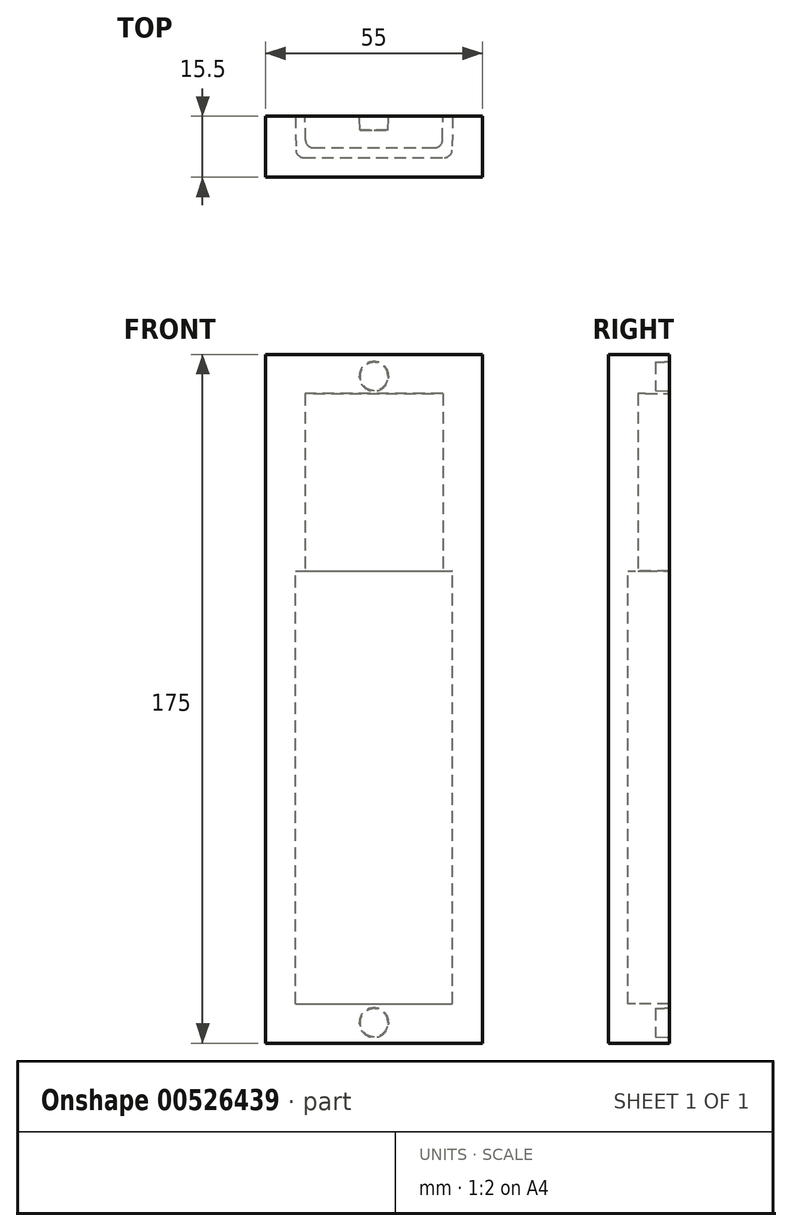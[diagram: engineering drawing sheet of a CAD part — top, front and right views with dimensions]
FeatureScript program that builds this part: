
annotation { "Feature Type Name" : "Feature", "Feature Type Description" : "" }
export const myFeature = defineFeature(function(context is Context, id is Id, definition is map)
    precondition{}
    {
        {
            var Q0;
            Q0=qCreatedBy(makeId("Top.planeOp"),FACE);
            var sketch = newSketch(context, id + "F0", { "sketchPlane" : qUnion([Q0])});
            skLineSegment(sketch, "E0.bottom", {"start": v(25, -13) * mm, "end": v(-25, -13) * mm});
            skLineSegment(sketch, "E0.top", {"start": v(25, 13) * mm, "end": v(-25, 13) * mm});
            skLineSegment(sketch, "E0.left", {"start": v(25, -13) * mm, "end": v(25, 13) * mm});
            skLineSegment(sketch, "E0.right", {"start": v(-25, -13) * mm, "end": v(-25, 13) * mm});
            skPoint(sketch, "E0.middle", {"position": v(0, 0) * mm});
            skSolve(sketch);
        }
        {
            var Q0;
            Q0=qSketchRegion(id+"F0",true);
            extrude(context, id + "F1", {"entities" : qUnion([Q0]), "depth" : 55 * mm, "offsetDistance" : 25 * mm});
        }
        {
            var Q0;
            Q0=makeQuery(id+"F1.opExtrude","CAP_FACE",FACE,{"disambiguationData":[OSD([sQuery(id+"F0.wireOp",EDGE,"E0.bottom"),sQuery(id+"F0.wireOp",EDGE,"E0.top"),sQuery(id+"F0.wireOp",EDGE,"E0.left"),sQuery(id+"F0.wireOp",EDGE,"E0.right")])],"isStart":true});
            var sketch = newSketch(context, id + "F2", { "sketchPlane" : qUnion([Q0])});
            skPoint(sketch, "E1.middle", {"position": v(0, 0) * mm});
            skLineSegment(sketch, "E2", {"start": v(17.36, -8) * mm, "end": v(17.5, 0) * mm});
            skLineSegment(sketch, "E3", {"start": v(-17.36, -8) * mm, "end": v(-17.5, 0) * mm});
            skLineSegment(sketch, "E4", {"start": v(-17.36, 8) * mm, "end": v(-17.5, 0) * mm});
            skLineSegment(sketch, "E5", {"start": v(17.36, 8) * mm, "end": v(17.5, 0) * mm});
            skLineSegment(sketch, "E6", {"start": v(-17.36, 8) * mm, "end": v(17.36, 8) * mm});
            skLineSegment(sketch, "E7", {"start": v(-17.36, -8) * mm, "end": v(17.36, -8) * mm});
            skSolve(sketch);
        }
        {
            var Q0;
            Q0=qSketchRegion(id+"F2",true);
            extrude(context, id + "F3", {"entities" : qUnion([Q0]), "operationType" : NewBodyOperationType.REMOVE, "oppositeDirection" : true, "depth" : 45 * mm, "offsetDistance" : 25 * mm});
        }
        {
            var Q0;
            Q0=makeQuery(id+"F3.boolean.opBoolean","COPY",EDGE,{"derivedFrom":makeQuery(id+"F3.opExtrude","SWEPT_EDGE",EDGE,{"disambiguationData":[OSD([sQuery(id+"F2.wireOp",EDGE,"E3"),sQuery(id+"F2.wireOp",EDGE,"E7")])]})});
            var Q1;
            Q1=makeQuery(id+"F3.boolean.opBoolean","COPY",EDGE,{"derivedFrom":makeQuery(id+"F3.opExtrude","SWEPT_EDGE",EDGE,{"disambiguationData":[OSD([sQuery(id+"F2.wireOp",EDGE,"E2"),sQuery(id+"F2.wireOp",EDGE,"E7")])]})});
            fillet(context, id + "F4", {"entities" : qUnion([Q0, Q1]), "radius" : 2 * mm, "tangentPropagation" : true, "allowEdgeOverflow" : false});
        }
        {
            var Q0;
            Q0=makeQuery(id+"F3.boolean.opBoolean","COPY",EDGE,{"derivedFrom":makeQuery(id+"F3.opExtrude","SWEPT_EDGE",EDGE,{"disambiguationData":[OSD([sQuery(id+"F2.wireOp",EDGE,"E4"),sQuery(id+"F2.wireOp",EDGE,"E6")])]})});
            var Q1;
            Q1=makeQuery(id+"F3.boolean.opBoolean","COPY",EDGE,{"derivedFrom":makeQuery(id+"F3.opExtrude","SWEPT_EDGE",EDGE,{"disambiguationData":[OSD([sQuery(id+"F2.wireOp",EDGE,"E5"),sQuery(id+"F2.wireOp",EDGE,"E6")])]})});
            fillet(context, id + "F5", {"entities" : qUnion([Q0, Q1]), "radius" : 2 * mm, "tangentPropagation" : true, "allowEdgeOverflow" : false});
        }
        {
            var Q0;
            Q0=makeQuery(id+"F1.opExtrude","CAP_FACE",FACE,{"disambiguationData":[OSD([sQuery(id+"F0.wireOp",EDGE,"E0.bottom"),sQuery(id+"F0.wireOp",EDGE,"E0.top"),sQuery(id+"F0.wireOp",EDGE,"E0.left"),sQuery(id+"F0.wireOp",EDGE,"E0.right")])],"isStart":true});
            var sketch = newSketch(context, id + "F6", { "sketchPlane" : qUnion([Q0])});
            skLineSegment(sketch, "E8.bottom", {"start": v(27.5, -15.5) * mm, "end": v(-27.5, -15.5) * mm});
            skLineSegment(sketch, "E8.top", {"start": v(27.5, 15.5) * mm, "end": v(-27.5, 15.5) * mm});
            skLineSegment(sketch, "E8.left", {"start": v(27.5, -15.5) * mm, "end": v(27.5, 15.5) * mm});
            skLineSegment(sketch, "E8.right", {"start": v(-27.5, -15.5) * mm, "end": v(-27.5, 15.5) * mm});
            skPoint(sketch, "E8.middle", {"position": v(0, 0) * mm});
            skSolve(sketch);
        }
        {
            var Q0;
            Q0=qSketchRegion(id+"F6",true);
            extrude(context, id + "F7", {"entities" : qUnion([Q0]), "operationType" : NewBodyOperationType.ADD, "depth" : 120 * mm, "offsetDistance" : 25 * mm});
        }
        {
            var Q0;
            {var subQ0=sQuery(id+"F6.wireOp",EDGE,"E8.bottom");var subQ1=sQuery(id+"F6.wireOp",EDGE,"E8.top");var subQ2=sQuery(id+"F6.wireOp",EDGE,"E8.left");var subQ3=sQuery(id+"F6.wireOp",EDGE,"E8.right");Q0=makeQuery(id+"F7.boolean.opBoolean","SPLIT",FACE,{"disambiguationData":[TD([makeQuery(id+"F1.opExtrude","SWEPT_FACE",FACE,{"disambiguationData":[OSD([sQuery(id+"F0.wireOp",EDGE,"E0.bottom")])]})])],"derivedFrom":makeQuery(id+"F7.opExtrude","CAP_FACE",FACE,{"disambiguationData":[OSD([subQ0,subQ1,subQ2,subQ3])],"isStart":true})});}
            var sketch = newSketch(context, id + "F8", { "sketchPlane" : qUnion([Q0])});
            skPoint(sketch, "E9.middle", {"position": v(0, 0) * mm});
            skLineSegment(sketch, "E10", {"start": v(-20, 0) * mm, "end": v(-19.82, -10.5) * mm});
            skLineSegment(sketch, "E11", {"start": v(20, 0) * mm, "end": v(19.82, -10.5) * mm});
            skLineSegment(sketch, "E12", {"start": v(19.82, 10.5) * mm, "end": v(20, 0) * mm});
            skLineSegment(sketch, "E13", {"start": v(-20, 0) * mm, "end": v(-19.82, 10.5) * mm});
            skLineSegment(sketch, "E14", {"start": v(-19.82, -10.5) * mm, "end": v(19.82, -10.5) * mm});
            skLineSegment(sketch, "E15", {"start": v(-19.82, 10.5) * mm, "end": v(19.82, 10.5) * mm});
            skSolve(sketch);
        }
        {
            var Q0;
            Q0=qSketchRegion(id+"F8",true);
            extrude(context, id + "F9", {"entities" : qUnion([Q0]), "operationType" : NewBodyOperationType.REMOVE, "oppositeDirection" : true, "depth" : 110 * mm, "offsetDistance" : 25 * mm});
        }
        {
            var Q0;
            Q0=makeQuery(id+"F9.boolean.opBoolean","COPY",EDGE,{"derivedFrom":makeQuery(id+"F9.opExtrude","SWEPT_EDGE",EDGE,{"disambiguationData":[OSD([sQuery(id+"F8.wireOp",EDGE,"E10"),sQuery(id+"F8.wireOp",EDGE,"E14")])]})});
            var Q1;
            Q1=makeQuery(id+"F9.boolean.opBoolean","COPY",EDGE,{"derivedFrom":makeQuery(id+"F9.opExtrude","SWEPT_EDGE",EDGE,{"disambiguationData":[OSD([sQuery(id+"F8.wireOp",EDGE,"E11"),sQuery(id+"F8.wireOp",EDGE,"E14")])]})});
            var Q2;
            Q2=makeQuery(id+"F9.boolean.opBoolean","COPY",EDGE,{"derivedFrom":makeQuery(id+"F9.opExtrude","SWEPT_EDGE",EDGE,{"disambiguationData":[OSD([sQuery(id+"F8.wireOp",EDGE,"E13"),sQuery(id+"F8.wireOp",EDGE,"E15")])]})});
            var Q3;
            Q3=makeQuery(id+"F9.boolean.opBoolean","COPY",EDGE,{"derivedFrom":makeQuery(id+"F9.opExtrude","SWEPT_EDGE",EDGE,{"disambiguationData":[OSD([sQuery(id+"F8.wireOp",EDGE,"E12"),sQuery(id+"F8.wireOp",EDGE,"E15")])]})});
            fillet(context, id + "F10", {"entities" : qUnion([Q0, Q1, Q2, Q3]), "radius" : 2 * mm, "tangentPropagation" : true, "allowEdgeOverflow" : false});
        }
        {
            var Q0;
            Q0=qCreatedBy(makeId("Front.planeOp"),FACE);
            var sketch = newSketch(context, id + "F11", { "sketchPlane" : qUnion([Q0])});
            skLineSegment(sketch, "E16.bottom", {"start": v(-94.89, 86.67) * mm, "end": v(98.98, 86.67) * mm});
            skLineSegment(sketch, "E16.top", {"start": v(-94.89, -148.46) * mm, "end": v(98.98, -148.46) * mm});
            skLineSegment(sketch, "E16.left", {"start": v(-94.89, 86.67) * mm, "end": v(-94.89, -148.46) * mm});
            skLineSegment(sketch, "E16.right", {"start": v(98.98, 86.67) * mm, "end": v(98.98, -148.46) * mm});
            skSolve(sketch);
        }
        {
            var Q0;
            Q0=qSketchRegion(id+"F11",true);
            extrude(context, id + "F12", {"entities" : qUnion([Q0]), "operationType" : NewBodyOperationType.REMOVE, "endBound" : BoundingType.THROUGH_ALL, "oppositeDirection" : true, "depth" : 25 * mm, "offsetDistance" : 25 * mm});
        }
        {
            var Q0;
            Q0=makeQuery(id+"F12.boolean.opBoolean","COPY",FACE,{"derivedFrom":makeQuery(id+"F12.opExtrude","CAP_FACE",FACE,{"disambiguationData":[OSD([sQuery(id+"F11.wireOp",EDGE,"E16.bottom"),sQuery(id+"F11.wireOp",EDGE,"E16.top"),sQuery(id+"F11.wireOp",EDGE,"E16.left"),sQuery(id+"F11.wireOp",EDGE,"E16.right")])],"isStart":true})});
            var sketch = newSketch(context, id + "F13", { "sketchPlane" : qUnion([Q0])});
            skCircle(sketch, "E17", {"center": v(0, 49.44) * mm, "radius": 3.75 * mm});
            skCircle(sketch, "E18", {"center": v(0, -114.77) * mm, "radius": 3.75 * mm});
            skSolve(sketch);
        }
        {
            var Q0;
            Q0=makeQuery(id+"F13.imprint","IMPRINT",FACE,{"disambiguationData":[TD([[makeQuery(id+"F13.imprint","IMPRINT",EDGE,{"derivedFrom":sQuery(id+"F13.wireOp",EDGE,"E17")}),1.0]])]});
            var Q1;
            Q1=makeQuery(id+"F13.imprint","IMPRINT",FACE,{"disambiguationData":[TD([[makeQuery(id+"F13.imprint","IMPRINT",EDGE,{"derivedFrom":sQuery(id+"F13.wireOp",EDGE,"E18")}),1.0]])]});
            extrude(context, id + "F14", {"entities" : qUnion([Q0, Q1]), "operationType" : NewBodyOperationType.REMOVE, "oppositeDirection" : true, "depth" : 3.5 * mm, "offsetDistance" : 25 * mm, "hasDraft" : true, "draftAngle" : 3 * degree, "draftPullDirection" : true});
        }
        {
            var Q0;
            {var subQ0=sQuery(id+"F6.wireOp",EDGE,"E8.bottom");var subQ1=sQuery(id+"F6.wireOp",EDGE,"E8.top");var subQ2=sQuery(id+"F6.wireOp",EDGE,"E8.left");var subQ3=sQuery(id+"F6.wireOp",EDGE,"E8.right");Q0=makeQuery(id+"F7.boolean.opBoolean","SPLIT",FACE,{"disambiguationData":[TD([makeQuery(id+"F1.opExtrude","SWEPT_FACE",FACE,{"disambiguationData":[OSD([sQuery(id+"F0.wireOp",EDGE,"E0.bottom")])]})])],"derivedFrom":makeQuery(id+"F7.opExtrude","CAP_FACE",FACE,{"disambiguationData":[OSD([subQ0,subQ1,subQ2,subQ3])],"isStart":true})});}
            var Q1;
            Q1=makeQuery(id+"F1.opExtrude","CAP_FACE",FACE,{"disambiguationData":[OSD([sQuery(id+"F0.wireOp",EDGE,"E0.bottom"),sQuery(id+"F0.wireOp",EDGE,"E0.top"),sQuery(id+"F0.wireOp",EDGE,"E0.left"),sQuery(id+"F0.wireOp",EDGE,"E0.right")])],"isStart":false});
            extrude(context, id + "F15", {"entities" : qUnion([Q0]), "operationType" : NewBodyOperationType.ADD, "endBound" : BoundingType.UP_TO_SURFACE, "depth" : 25 * mm, "endBoundEntityFace" : qUnion([Q1]), "offsetDistance" : 25 * mm});
        }
    });
